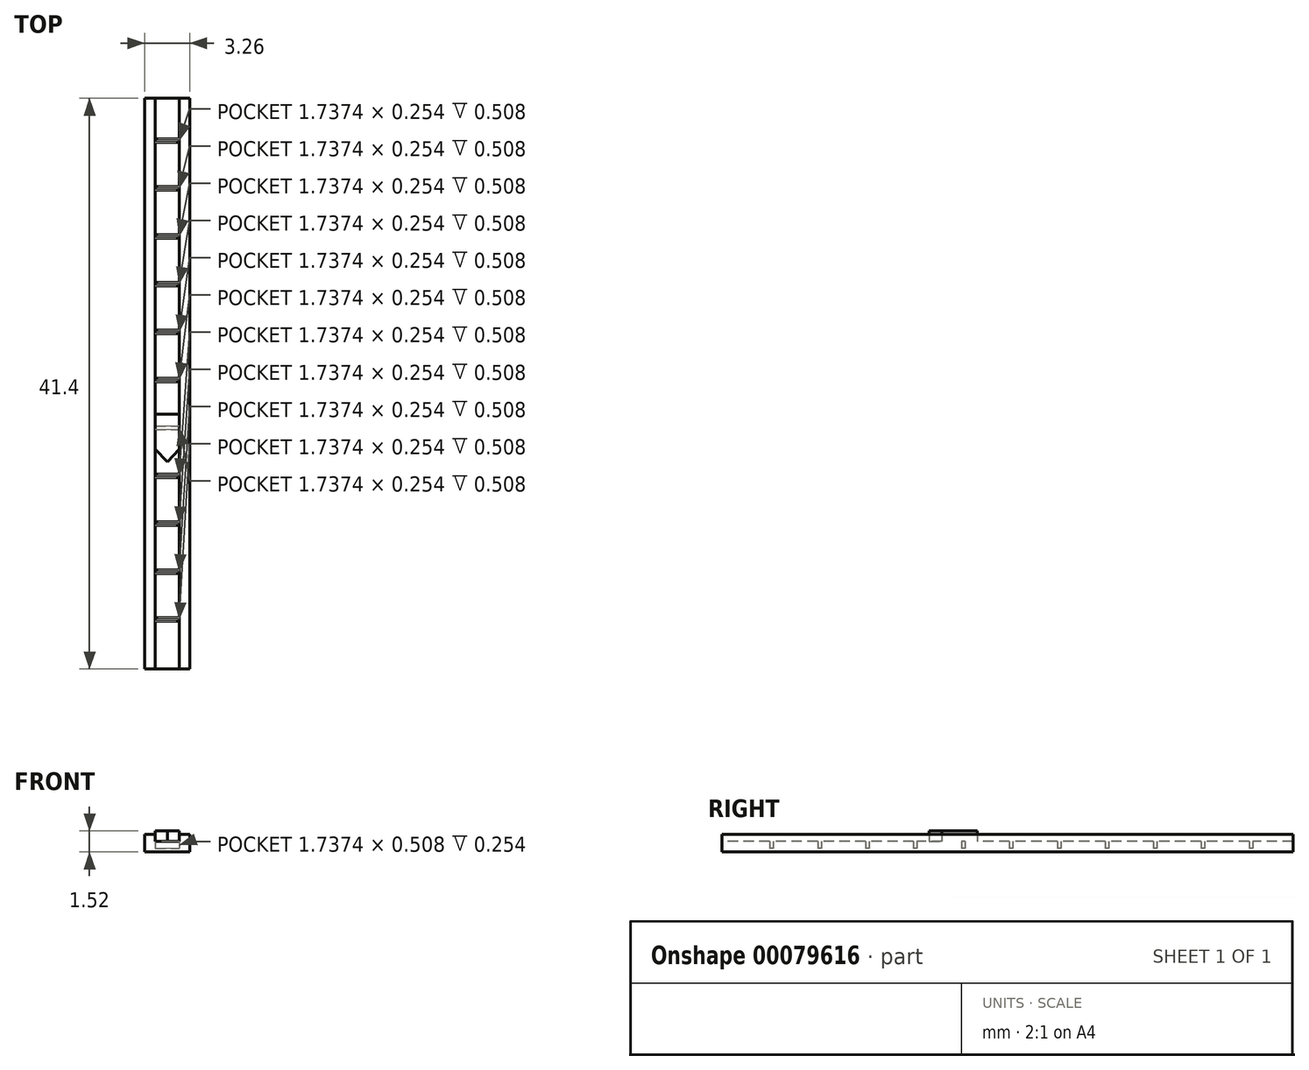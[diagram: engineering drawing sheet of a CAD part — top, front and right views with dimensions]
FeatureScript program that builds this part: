
annotation { "Feature Type Name" : "Feature", "Feature Type Description" : "" }
export const myFeature = defineFeature(function(context is Context, id is Id, definition is map)
    precondition{}
    {
        {
            var Q0;
            Q0=qCreatedBy(makeId("Top.planeOp"),FACE);
            var sketch = newSketch(context, id + "F0", { "sketchPlane" : qUnion([Q0])});
            skLineSegment(sketch, "E0.bottom", {"start": v(0, 0.16) * mm, "end": v(1.74, 0.16) * mm});
            skLineSegment(sketch, "E0.top", {"start": v(0, -41.24) * mm, "end": v(1.74, -41.24) * mm});
            skLineSegment(sketch, "E0.left", {"start": v(0, 0.16) * mm, "end": v(0, -41.24) * mm});
            skLineSegment(sketch, "E0.right", {"start": v(1.74, 0.16) * mm, "end": v(1.74, -41.24) * mm});
            skSolve(sketch);
        }
        {
            var Q0;
            Q0 = qSketchRegion(id + "F0", true);
            extrude(context, id + "F1", {"entities" : qUnion([Q0]), "depth" : 0.76 * mm});
        }
        {
            var Q0;
            Q0=makeQuery(id+"F1.opExtrude","CAP_FACE",FACE,{"disambiguationData":[OSD([sQuery(id+"F0.wireOp",EDGE,"E0.bottom"),sQuery(id+"F0.wireOp",EDGE,"E0.top"),sQuery(id+"F0.wireOp",EDGE,"E0.left"),sQuery(id+"F0.wireOp",EDGE,"E0.right")])],"isStart":false});
            var sketch = newSketch(context, id + "F2", { "sketchPlane" : qUnion([Q0])});
            skLineSegment(sketch, "E1.left", {"start": v(0, -25.28) * mm, "end": v(0, -22.73) * mm});
            skLineSegment(sketch, "E1.right", {"start": v(1.74, -25.28) * mm, "end": v(1.74, -22.73) * mm});
            skPoint(sketch, "E2.endSnap0", {"position": v(0.87, -22.73) * mm});
            skPoint(sketch, "E3.start.orphan", {"position": v(0.87, -27.97) * mm});
            skLineSegment(sketch, "E4", {"start": v(0, -22.73) * mm, "end": v(1.74, -22.73) * mm});
            skLineSegment(sketch, "E5", {"start": v(0.87, -26.2) * mm, "end": v(1.74, -25.28) * mm});
            skLineSegment(sketch, "E6", {"start": v(0, -25.28) * mm, "end": v(0.87, -26.2) * mm});
            skPoint(sketch, "E7.orphan", {"position": v(0, -26.2) * mm});
            skPoint(sketch, "E8.orphan", {"position": v(1.74, -26.2) * mm});
            skSolve(sketch);
        }
        {
            var Q0;
            Q0 = qSketchRegion(id + "F2", true);
            extrude(context, id + "F3", {"entities" : qUnion([Q0]), "operationType" : NewBodyOperationType.ADD, "depth" : 0.76 * mm});
        }
        {
            var Q0;
            {var subQ0=sQuery(id+"F0.wireOp",EDGE,"E0.right");var subQ1=sQuery(id+"F0.wireOp",EDGE,"E0.left");var subQ2=sQuery(id+"F0.wireOp",EDGE,"E0.bottom");Q0=makeQuery(id+"F3.boolean.opBoolean","SPLIT",FACE,{"disambiguationData":[TD([makeQuery(id+"F1.opExtrude","SWEPT_FACE",FACE,{"disambiguationData":[OSD([subQ2])]})])],"derivedFrom":makeQuery(id+"F1.opExtrude","CAP_FACE",FACE,{"disambiguationData":[OSD([subQ2,sQuery(id+"F0.wireOp",EDGE,"E0.top"),subQ1,subQ0])],"isStart":false})});}
            var sketch = newSketch(context, id + "F4", { "sketchPlane" : qUnion([Q0])});
            skLineSegment(sketch, "E9.bottom", {"start": v(-0.2, -37.51) * mm, "end": v(4.36, -37.51) * mm});
            skLineSegment(sketch, "E9.left", {"start": v(-0.2, -37.51) * mm, "end": v(-0.2, -37.77) * mm});
            skLineSegment(sketch, "E9.right", {"start": v(4.36, -37.51) * mm, "end": v(4.36, -37.77) * mm});
            skLineSegment(sketch, "E10.left", {"start": v(-0.78, -19.2) * mm, "end": v(-0.78, -19.45) * mm});
            skLineSegment(sketch, "E11.1.0.0", {"start": v(-0.22, -34.3) * mm, "end": v(4.35, -34.3) * mm});
            skLineSegment(sketch, "E11.1.0.1", {"start": v(-0.22, -34.04) * mm, "end": v(4.35, -34.04) * mm});
            skLineSegment(sketch, "E11.1.0.2", {"start": v(4.35, -34.04) * mm, "end": v(4.35, -34.3) * mm});
            skLineSegment(sketch, "E11.1.0.3", {"start": v(-0.22, -34.04) * mm, "end": v(-0.22, -34.3) * mm});
            skLineSegment(sketch, "E11.2.0.0", {"start": v(-0.23, -30.82) * mm, "end": v(4.34, -30.82) * mm});
            skLineSegment(sketch, "E11.2.0.1", {"start": v(-0.23, -30.56) * mm, "end": v(4.34, -30.56) * mm});
            skLineSegment(sketch, "E11.2.0.2", {"start": v(4.34, -30.56) * mm, "end": v(4.34, -30.82) * mm});
            skLineSegment(sketch, "E11.2.0.3", {"start": v(-0.23, -30.56) * mm, "end": v(-0.23, -30.82) * mm});
            skLineSegment(sketch, "E11.direction1", {"start": v(-0.2, -37.77) * mm, "end": v(-0.22, -34.3) * mm, "construction": true});
            skLineSegment(sketch, "E12.0.3.0", {"start": v(-0.24, -27.34) * mm, "end": v(4.33, -27.34) * mm});
            skLineSegment(sketch, "E12.3.3.0", {"start": v(-0.24, -27.09) * mm, "end": v(4.33, -27.09) * mm});
            skLineSegment(sketch, "E12.6.3.0", {"start": v(4.33, -27.09) * mm, "end": v(4.33, -27.34) * mm});
            skLineSegment(sketch, "E12.9.3.0", {"start": v(-0.24, -27.09) * mm, "end": v(-0.24, -27.34) * mm});
            skLineSegment(sketch, "E12.0.4.0", {"start": v(-0.25, -23.87) * mm, "end": v(4.32, -23.87) * mm});
            skLineSegment(sketch, "E12.3.4.0", {"start": v(-0.25, -23.61) * mm, "end": v(4.32, -23.61) * mm});
            skLineSegment(sketch, "E12.6.4.0", {"start": v(4.32, -23.61) * mm, "end": v(4.32, -23.87) * mm});
            skLineSegment(sketch, "E12.9.4.0", {"start": v(-0.25, -23.61) * mm, "end": v(-0.25, -23.87) * mm});
            skLineSegment(sketch, "E13", {"start": v(-0.2, -37.77) * mm, "end": v(4.36, -37.77) * mm});
            skLineSegment(sketch, "E14.0.5.0", {"start": v(-0.27, -20.4) * mm, "end": v(4.3, -20.4) * mm});
            skLineSegment(sketch, "E14.3.5.0", {"start": v(-0.27, -20.14) * mm, "end": v(4.3, -20.14) * mm});
            skLineSegment(sketch, "E14.6.5.0", {"start": v(4.3, -20.14) * mm, "end": v(4.3, -20.4) * mm});
            skLineSegment(sketch, "E14.9.5.0", {"start": v(-0.27, -20.14) * mm, "end": v(-0.27, -20.4) * mm});
            skLineSegment(sketch, "E14.0.6.0", {"start": v(-0.28, -16.92) * mm, "end": v(4.3, -16.92) * mm});
            skLineSegment(sketch, "E14.3.6.0", {"start": v(-0.28, -16.67) * mm, "end": v(4.3, -16.67) * mm});
            skLineSegment(sketch, "E14.6.6.0", {"start": v(4.3, -16.67) * mm, "end": v(4.3, -16.92) * mm});
            skLineSegment(sketch, "E14.9.6.0", {"start": v(-0.28, -16.67) * mm, "end": v(-0.28, -16.92) * mm});
            skLineSegment(sketch, "E14.0.7.0", {"start": v(-0.29, -13.44) * mm, "end": v(4.28, -13.44) * mm});
            skLineSegment(sketch, "E14.3.7.0", {"start": v(-0.29, -13.2) * mm, "end": v(4.28, -13.2) * mm});
            skLineSegment(sketch, "E14.6.7.0", {"start": v(4.28, -13.2) * mm, "end": v(4.28, -13.44) * mm});
            skLineSegment(sketch, "E14.9.7.0", {"start": v(-0.29, -13.2) * mm, "end": v(-0.29, -13.44) * mm});
            skLineSegment(sketch, "E14.0.8.0", {"start": v(-0.3, -9.97) * mm, "end": v(4.27, -9.97) * mm});
            skLineSegment(sketch, "E14.3.8.0", {"start": v(-0.3, -9.72) * mm, "end": v(4.27, -9.72) * mm});
            skLineSegment(sketch, "E14.6.8.0", {"start": v(4.27, -9.72) * mm, "end": v(4.27, -9.97) * mm});
            skLineSegment(sketch, "E14.9.8.0", {"start": v(-0.3, -9.72) * mm, "end": v(-0.3, -9.97) * mm});
            skLineSegment(sketch, "E14.0.9.0", {"start": v(-0.31, -6.5) * mm, "end": v(4.26, -6.5) * mm});
            skLineSegment(sketch, "E14.3.9.0", {"start": v(-0.31, -6.24) * mm, "end": v(4.26, -6.24) * mm});
            skLineSegment(sketch, "E14.6.9.0", {"start": v(4.26, -6.24) * mm, "end": v(4.26, -6.5) * mm});
            skLineSegment(sketch, "E14.9.9.0", {"start": v(-0.31, -6.24) * mm, "end": v(-0.31, -6.5) * mm});
            skLineSegment(sketch, "E14.0.10.0", {"start": v(-0.32, -3.02) * mm, "end": v(4.25, -3.02) * mm});
            skLineSegment(sketch, "E14.3.10.0", {"start": v(-0.32, -2.77) * mm, "end": v(4.25, -2.77) * mm});
            skLineSegment(sketch, "E14.6.10.0", {"start": v(4.25, -2.77) * mm, "end": v(4.25, -3.02) * mm});
            skLineSegment(sketch, "E14.9.10.0", {"start": v(-0.32, -2.77) * mm, "end": v(-0.32, -3.02) * mm});
            skSolve(sketch);
        }
        {
            var Q0;
            Q0 = qSketchRegion(id + "F4", true);
            extrude(context, id + "F5", {"entities" : qUnion([Q0]), "operationType" : NewBodyOperationType.REMOVE, "oppositeDirection" : true, "depth" : 0.5 * mm});
        }
        {
            var Q0;
            Q0=qCreatedBy(makeId("Top.planeOp"),FACE);
            var sketch = newSketch(context, id + "F6", { "sketchPlane" : qUnion([Q0])});
            skLineSegment(sketch, "E15.bottom", {"start": v(0, -41.24) * mm, "end": v(-0.76, -41.24) * mm});
            skLineSegment(sketch, "E15.top", {"start": v(0, 0.16) * mm, "end": v(-0.76, 0.16) * mm});
            skLineSegment(sketch, "E15.left", {"start": v(0, -41.24) * mm, "end": v(0, 0.16) * mm});
            skLineSegment(sketch, "E15.right", {"start": v(-0.76, -41.24) * mm, "end": v(-0.76, 0.16) * mm});
            skLineSegment(sketch, "E16.bottom", {"start": v(1.74, -41.24) * mm, "end": v(2.5, -41.24) * mm});
            skLineSegment(sketch, "E16.top", {"start": v(1.74, 0.16) * mm, "end": v(2.5, 0.16) * mm});
            skLineSegment(sketch, "E16.left", {"start": v(1.74, -41.24) * mm, "end": v(1.74, 0.16) * mm});
            skLineSegment(sketch, "E16.right", {"start": v(2.5, -41.24) * mm, "end": v(2.5, 0.16) * mm});
            skSolve(sketch);
        }
        {
            var Q0;
            Q0 = qSketchRegion(id + "F6", true);
            extrude(context, id + "F7", {"entities" : qUnion([Q0]), "operationType" : NewBodyOperationType.ADD, "depth" : 1.27 * mm});
        }
    });
